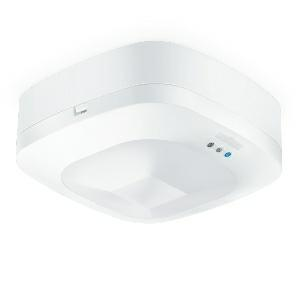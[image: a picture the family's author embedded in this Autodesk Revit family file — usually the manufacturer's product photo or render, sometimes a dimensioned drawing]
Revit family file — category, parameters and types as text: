
# Revit family: hf_360_751302
name_source: partatom
category: Elektroinstallationen
revit_build: Autodesk Revit 2016 (Build: 20190508_0715(x64)
units: mm (PartAtom-declared; Revit-internal decimal feet)

## family parameters
Basisbauteil = Fläche
Beim Laden mit Abzugskörper schneiden = Nein
Bemaßung runder Anschluss = Durchmesser verwenden
Beschriftungsausrichtung beibehalten = Nein
Gemeinsam genutzt = Nein
Raumberechnungspunkt = Nein
Teiletyp = Normal

## types (1)
- HF 360
    Apparent Load = 0 VA
    Beschreibung = Type: Presence detector; Dimensions (L x W x H): 51 x 120 x 120 mm; Mains power supply: 230 V / 50 – 60 Hz; Sensor Technology: High frequency; Application, place: Indoors; Application, room: function room / ancillary room, kitchenette, stairwell, WC / washroom, Indoors; Installation site: ceiling; Installation: Surface wiring; HF-system: 5,8 GHz; Electronic scalability: Yes; Mechanical scalability: No; Mounting height: 2,50 – 3,50 m; Optimum mounting height: 2,8 m; Detection: also through glass, wood and stud walls; Detection angle: 360 °; Angle of aperture: 160 °; Sneak-by guard: Yes; Capability of masking out individual segments: Yes; Reach, detail: 1 or 2 detection directions can be masked out by stickers for adjustment to the room situation.; Reach, radial: Ø 12 m (113 m²); Reach, tangential: Ø 12 m (113 m²); Twilight setting TEACH: Yes; Twilight setting: 10 – 1000 lx; Time setting: 30 sec – 30 min; Constant-lighting control: No; Basic light level function: No; Functions: Normal / test mode, Semi-/fully automatic, Pushbutton / switch mode, Manual ON / ON-OFF; Settings via: Remote control, DIP switches, Potentiometers, Smart Remote; With remote control: No; Interconnection: Yes; Type of interconnection: Master/slave, Master/master; IP-rating: IP20; Material: Plastic; Ambient temperature: -25 – 55 °C; Colour: white; Colour, RAL: 9010; Manufacturer's Warranty: 5 years; Version: COM1 AP; PU1, EAN: 4007841751302
    Height = 120 mm  [stored 0.393701 ft]
    Hersteller = Steinel
    Length = 51 mm
    Maximum range = 6.001 m
    ModVariant = Nein
    Modell = 751302
    Mounting Place = Ceiling
    Mounting Type = Surface mounted
    Number of Poles = 1
    OnlyDefault = Ja
    Power Factor = 1
    Product Name = HF 360
    Product group = Sensor-switched outdoor light
    ProductGroupID = 3
    Protection Class = Protection class
    Protection Degree = IP 20
    RlxData = <blob elided: 129973 chars, md5=2f79d549>
    Sensor characteristics = Circular 300°-360°
    Sensor type = Passive (infrared)
    SensorDataFile = <blob elided: 8551 chars, md5=1477a78d>
    Type of entry = Motion
    Typenbild = produkt1_751302.jpg
    Typenkommentare = Product without accessories
    URL = http://relux.com
    VarID = ---
    Voltage = 0 V
    Vorgabe-Ansicht = 1800 mm
    Weight = 0.00 kg
    Width = 120 mm  [stored 0.393701 ft]

note: [stored X ft] marks values corroborated as IEEE doubles in the binary element streams (Revit-internal decimal feet)

## geometry (parser evidence)
native form markers: Blend x4, Sweep x17
no freeform markers — native parametric forms only
